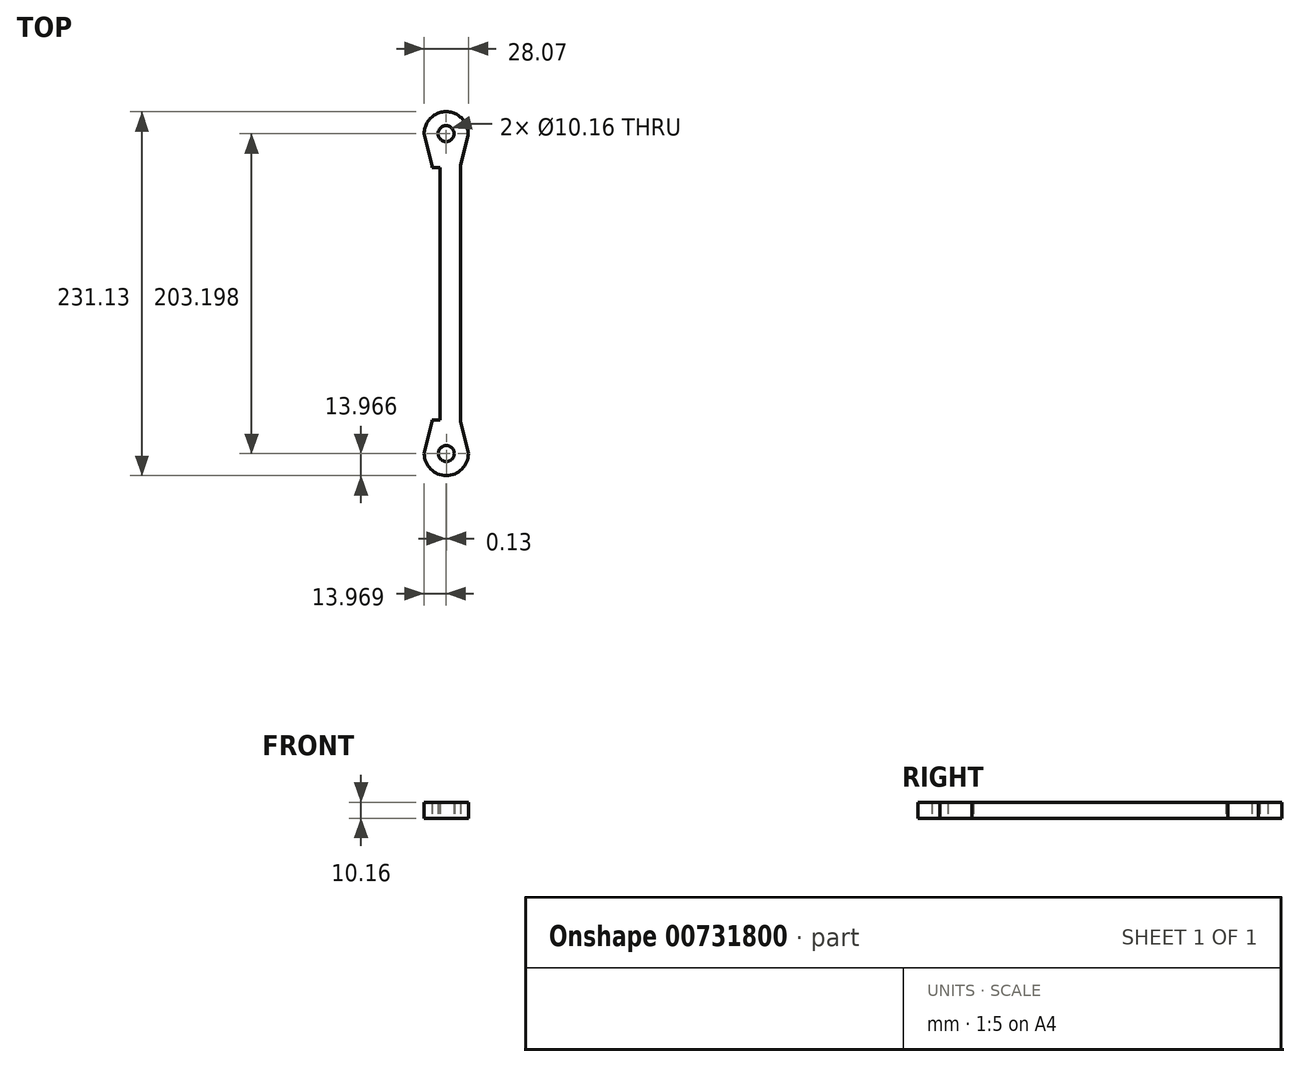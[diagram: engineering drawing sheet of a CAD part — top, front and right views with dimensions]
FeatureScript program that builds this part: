
annotation { "Feature Type Name" : "Feature", "Feature Type Description" : "" }
export const myFeature = defineFeature(function(context is Context, id is Id, definition is map)
    precondition{}
    {
        {
            var Q0;
            Q0=qCreatedBy(makeId("Top.planeOp"),FACE);
            var sketch = newSketch(context, id + "F0", { "sketchPlane" : qUnion([Q0])});
            skLineSegment(sketch, "E0", {"start": v(6.72, 103.7) * mm, "end": v(6.72, -58.85) * mm});
            skLineSegment(sketch, "E1", {"start": v(6.72, 103.7) * mm, "end": v(-11.06, 103.7) * mm});
            skLineSegment(sketch, "E2", {"start": v(-11.06, 103.7) * mm, "end": v(-11.06, -58.85) * mm});
            skLineSegment(sketch, "E3", {"start": v(-11.06, -58.85) * mm, "end": v(6.72, -58.85) * mm});
            skLineSegment(sketch, "E4", {"start": v(-2.17, -58.85) * mm, "end": v(-2.17, -74.1) * mm});
            skCircle(sketch, "E5", {"center": v(-2.17, -79.17) * mm, "radius": 5.08 * mm});
            skCircle(sketch, "E6", {"center": v(-2.17, -79.17) * mm, "radius": 13.97 * mm});
            skLineSegment(sketch, "E7", {"start": v(-16.14, -79.17) * mm, "end": v(-11.06, -58.85) * mm});
            skLineSegment(sketch, "E8", {"start": v(11.8, -79.17) * mm, "end": v(6.72, -58.85) * mm});
            skLineSegment(sketch, "E9", {"start": v(-2.17, 103.7) * mm, "end": v(-2.17, 118.95) * mm});
            skLineSegment(sketch, "E10", {"start": v(-2.17, 118.95) * mm, "end": v(-2.43, 129.1) * mm});
            skCircle(sketch, "E11", {"center": v(-2.3, 124.02) * mm, "radius": 5.08 * mm});
            skCircle(sketch, "E12", {"center": v(-2.3, 124.02) * mm, "radius": 13.97 * mm});
            skLineSegment(sketch, "E13", {"start": v(-16.27, 124.02) * mm, "end": v(11.67, 124.02) * mm});
            skLineSegment(sketch, "E14", {"start": v(-11.06, 103.7) * mm, "end": v(-16.27, 124.02) * mm});
            skLineSegment(sketch, "E15", {"start": v(6.72, 103.7) * mm, "end": v(11.64, 123.18) * mm});
            skLineSegment(sketch, "E16", {"start": v(-11.06, 102.64) * mm, "end": v(-5.98, 102.64) * mm});
            skLineSegment(sketch, "E17", {"start": v(6.72, 102.64) * mm, "end": v(1.64, 102.64) * mm});
            skLineSegment(sketch, "E18", {"start": v(4.88, -58.85) * mm, "end": v(4.88, -57.79) * mm});
            skLineSegment(sketch, "E19", {"start": v(6.72, -57.79) * mm, "end": v(1.64, -57.79) * mm});
            skLineSegment(sketch, "E20", {"start": v(-11.06, -57.79) * mm, "end": v(-5.98, -57.79) * mm});
            skLineSegment(sketch, "E21", {"start": v(-5.98, -57.79) * mm, "end": v(-5.98, 102.64) * mm});
            skLineSegment(sketch, "E22", {"start": v(1.64, 102.64) * mm, "end": v(1.64, -57.79) * mm});
            skLineSegment(sketch, "E23", {"start": v(-5.98, 102.64) * mm, "end": v(1.64, 102.64) * mm});
            skLineSegment(sketch, "E24", {"start": v(-5.98, -57.79) * mm, "end": v(1.64, -57.79) * mm});
            skSolve(sketch);
        }
        {
            var Q0;
            Q0=makeQuery(id+"F0.imprint","IMPRINT",FACE,{"disambiguationData":[TD([[makeQuery(id+"F0.imprint","IMPRINT",EDGE,{"derivedFrom":sQuery(id+"F0.wireOp",EDGE,"E5")}),-1.0]])]});
            var Q1;
            {var subQ0=sQuery(id+"F0.wireOp",EDGE,"E18");Q1=makeQuery(id+"F0.imprint","IMPRINT",FACE,{"disambiguationData":[TD([[makeQuery(id+"F0.imprint","IMPRINT",EDGE,{"derivedFrom":subQ0}),1.0]])]});}
            var Q2;
            {var subQ5=sQuery(id+"F0.wireOp",EDGE,"E18");Q2=makeQuery(id+"F0.imprint","IMPRINT",FACE,{"disambiguationData":[TD([[makeQuery(id+"F0.imprint","IMPRINT",EDGE,{"derivedFrom":subQ5}),-1.0]])]});}
            var Q3;
            {var subQ0=sQuery(id+"F0.wireOp",EDGE,"E4");var subQ1=sQuery(id+"F0.wireOp",EDGE,"E3");var subQ2=makeQuery(id+"F0.imprint","INTERSECT",VERTEX,{"derivedFrom":[subQ1,subQ0]});Q3=makeQuery(id+"F0.imprint","IMPRINT",FACE,{"disambiguationData":[TD([[makeQuery(id+"F0.imprint","IMPRINT",EDGE,{"disambiguationData":[TD([[subQ2,-1.0]])],"derivedFrom":subQ1}),-1.0]])]});}
            var Q4;
            {var subQ1=sQuery(id+"F0.wireOp",EDGE,"E3");var subQ3=sQuery(id+"F0.wireOp",EDGE,"E4");var subQ4=makeQuery(id+"F0.imprint","INTERSECT",VERTEX,{"derivedFrom":[subQ1,subQ3]});Q4=makeQuery(id+"F0.imprint","IMPRINT",FACE,{"disambiguationData":[TD([[makeQuery(id+"F0.imprint","IMPRINT",EDGE,{"disambiguationData":[TD([[subQ4,-1.0]])],"derivedFrom":subQ3}),-1.0]])]});}
            var Q5;
            Q5=makeQuery(id+"F0.imprint","IMPRINT",FACE,{"disambiguationData":[TD([[makeQuery(id+"F0.imprint","IMPRINT",EDGE,{"derivedFrom":sQuery(id+"F0.wireOp",EDGE,"E21")}),-1.0]])]});
            var Q6;
            {var subQ6=sQuery(id+"F0.wireOp",EDGE,"E16");Q6=makeQuery(id+"F0.imprint","IMPRINT",FACE,{"disambiguationData":[TD([[makeQuery(id+"F0.imprint","IMPRINT",EDGE,{"derivedFrom":subQ6}),1.0]])]});}
            var Q7;
            {var subQ1=sQuery(id+"F0.wireOp",EDGE,"E1");var subQ3=sQuery(id+"F0.wireOp",EDGE,"E9");var subQ4=makeQuery(id+"F0.imprint","INTERSECT",VERTEX,{"derivedFrom":[subQ1,subQ3]});Q7=makeQuery(id+"F0.imprint","IMPRINT",FACE,{"disambiguationData":[TD([[makeQuery(id+"F0.imprint","IMPRINT",EDGE,{"disambiguationData":[TD([[subQ4,-1.0]])],"derivedFrom":subQ3}),-1.0]])]});}
            var Q8;
            {var subQ1=sQuery(id+"F0.wireOp",EDGE,"E1");var subQ3=sQuery(id+"F0.wireOp",EDGE,"E9");var subQ4=makeQuery(id+"F0.imprint","INTERSECT",VERTEX,{"derivedFrom":[subQ1,subQ3]});Q8=makeQuery(id+"F0.imprint","IMPRINT",FACE,{"disambiguationData":[TD([[makeQuery(id+"F0.imprint","IMPRINT",EDGE,{"disambiguationData":[TD([[subQ4,-1.0]])],"derivedFrom":subQ3}),1.0]])]});}
            var Q9;
            {var subQ1=sQuery(id+"F0.wireOp",EDGE,"E12");var subQ3=sQuery(id+"F0.wireOp",EDGE,"E15");var subQ9=makeQuery(id+"F0.imprint","INTERSECT",VERTEX,{"disambiguationData":[OD(1.0)],"derivedFrom":[subQ1,subQ3]});Q9=makeQuery(id+"F0.imprint","IMPRINT",FACE,{"disambiguationData":[TD([[makeQuery(id+"F0.imprint","IMPRINT",EDGE,{"disambiguationData":[TD([[subQ9,1.0]])],"derivedFrom":subQ1}),1.0]])]});}
            var Q10;
            {var subQ0=sQuery(id+"F0.wireOp",EDGE,"E14");var subQ2=sQuery(id+"F0.wireOp",EDGE,"E12");var subQ6=makeQuery(id+"F0.imprint","INTERSECT",VERTEX,{"derivedFrom":[subQ2,subQ0]});Q10=makeQuery(id+"F0.imprint","IMPRINT",FACE,{"disambiguationData":[TD([[makeQuery(id+"F0.imprint","IMPRINT",EDGE,{"disambiguationData":[TD([[subQ6,-1.0]])],"derivedFrom":subQ2}),1.0]])]});}
            var Q11;
            {var subQ4=sQuery(id+"F0.wireOp",EDGE,"E11");var subQ5=makeQuery(id+"F0.imprint","INTERSECT",VERTEX,{"derivedFrom":[sQuery(id+"F0.wireOp",EDGE,"E10"),subQ4]});Q11=makeQuery(id+"F0.imprint","IMPRINT",FACE,{"disambiguationData":[TD([[makeQuery(id+"F0.imprint","IMPRINT",EDGE,{"disambiguationData":[TD([[subQ5,1.0]])],"derivedFrom":subQ4}),-1.0]])]});}
            extrude(context, id + "F1", {"entities" : qUnion([Q0, Q1, Q2, Q3, Q4, Q5, Q6, Q7, Q8, Q9, Q10, Q11]), "depth" : 10.16 * mm, "offsetDistance" : 25.4 * mm});
        }
        {
            var Q0;
            Q0=makeQuery(id+"F1.opExtrude","SWEPT_FACE",FACE,{"disambiguationData":[OSD([sQuery(id+"F0.wireOp",EDGE,"E22")])]});
            extrude(context, id + "F2", {"entities" : qUnion([Q0]), "operationType" : NewBodyOperationType.ADD, "depth" : 5.08 * mm, "offsetDistance" : 25.4 * mm});
        }
    });
